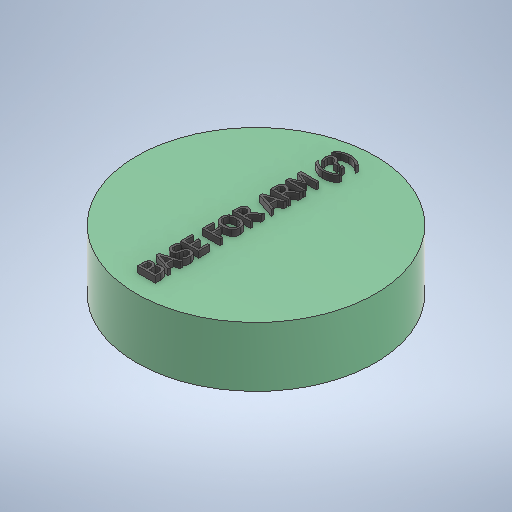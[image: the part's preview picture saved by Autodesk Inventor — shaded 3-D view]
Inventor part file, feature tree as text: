
AUTODESK INVENTOR PART (.ipt)
format: ipt  version: 2025.2 (Build 292293000, 293)  size: 513,024 bytes
history: native  units: mm
features: extrude x2, sketch x2
ambient origin geometry x8: Origin, YZ Plane, XZ Plane, XY Plane, X Axis, Y Axis, Z Axis, Center Point
bodies: Solid1 (feature_tree)
feature tree (4):
  extrude  "Extrusion1"  Depth=25.0mm TaperAngle=0.0deg
  extrude  "Extrusion2"  [1 undecoded]
  sketch  "Sketch1"  dims[d0=100.0mm d1=25.0mm d2=0.0mm]
  sketch  "Sketch2"  dims[d3=2.5mm d4=0.0mm]
note: 1 required parameter value undecoded (feature->parameter linkage not recoverable at this tier; creation-order binding heuristic only, values carry confidence <= 0.55)
